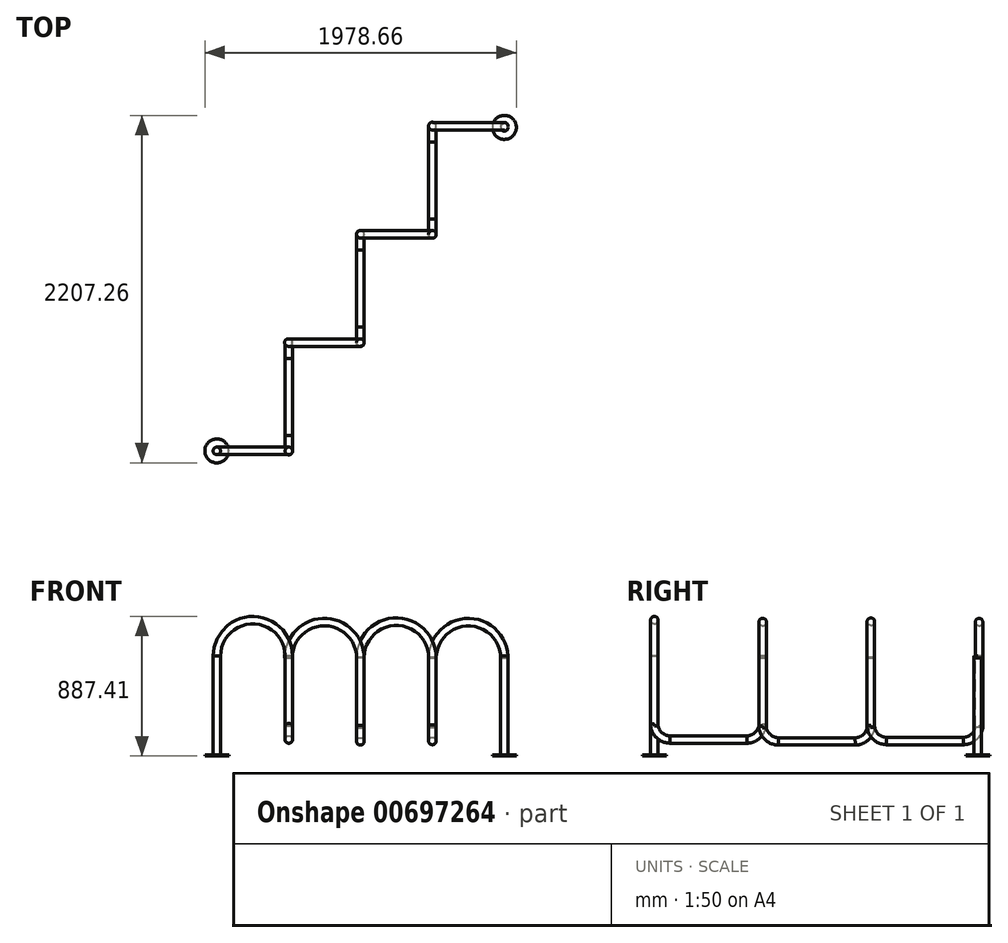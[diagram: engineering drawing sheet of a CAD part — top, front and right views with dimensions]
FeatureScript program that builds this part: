
annotation { "Feature Type Name" : "Feature", "Feature Type Description" : "" }
export const myFeature = defineFeature(function(context is Context, id is Id, definition is map)
    precondition{}
    {
        {
            var Q0;
            Q0=qCreatedBy(makeId("Top.planeOp"),FACE);
            var sketch = newSketch(context, id + "F0", { "sketchPlane" : qUnion([Q0])});
            skCircle(sketch, "E0", {"center": v(0, 0) * mm, "radius": 76.2 * mm});
            skCircle(sketch, "E1", {"center": v(0, 0) * mm, "radius": 23.81 * mm});
            skSolve(sketch);
        }
        {
            var Q0;
            Q0=makeQuery(id+"F0.imprint","IMPRINT",FACE,{"disambiguationData":[TD([[makeQuery(id+"F0.imprint","IMPRINT",EDGE,{"derivedFrom":sQuery(id+"F0.wireOp",EDGE,"E0")}),1.0]])]});
            extrude(context, id + "F1", {"entities" : qUnion([Q0]), "depth" : 6.35 * mm, "offsetDistance" : 25.4 * mm});
        }
        {
            var Q0;
            Q0=makeQuery(id+"F0.imprint","IMPRINT",FACE,{"disambiguationData":[TD([[makeQuery(id+"F0.imprint","IMPRINT",EDGE,{"derivedFrom":sQuery(id+"F0.wireOp",EDGE,"E1")}),1.0]])]});
            extrude(context, id + "F2", {"entities" : qUnion([Q0]), "operationType" : NewBodyOperationType.ADD, "depth" : 635 * mm, "offsetDistance" : 25.4 * mm});
        }
        {
            var Q0;
            Q0=qCreatedBy(makeId("Front.planeOp"),FACE);
            var sketch = newSketch(context, id + "F3", { "sketchPlane" : qUnion([Q0])});
            skArc(sketch, "E2", {"start": v(457.2, 635) * mm, "mid": v(228.6, 863.6) * mm, "end": v(0, 635) * mm});
            skLineSegment(sketch, "E3", {"start": v(0, 0) * mm, "end": v(0, 635) * mm});
            skLineSegment(sketch, "E4", {"start": v(457.2, 635) * mm, "end": v(457.2, 228.6) * mm});
            skLineSegment(sketch, "E5", {"start": v(228.6, 863.6) * mm, "end": v(228.6, 0) * mm, "construction": true});
            skLineSegment(sketch, "E6", {"start": v(228.6, 863.6) * mm, "end": v(951.54, 863.6) * mm, "construction": true});
            skSolve(sketch);
        }
        {
            var Q0;
            Q0=makeQuery(id+"F2.opExtrude","CAP_FACE",FACE,{"disambiguationData":[OSD([sQuery(id+"F0.wireOp",EDGE,"E1")])],"isStart":false});
            var Q1;
            Q1=sQuery(id+"F3.wireOp",EDGE,"E2");
            sweep(context, id + "F4", {"profiles" : qUnion([Q0]), "path" : qUnion([Q1])});
        }
        {
            var Q0;
            Q0=makeQuery(id+"F4.opSweep","CAP_FACE",FACE,{"disambiguationData":[OSD([sQuery(id+"F0.wireOp",EDGE,"E1"),sQuery(id+"F3.wireOp",VERTEX,"E2.start")])],"isStart":false});
            var sketch = newSketch(context, id + "F5", { "sketchPlane" : qUnion([Q0])});
            skCircle(sketch, "E7.0", {"center": v(457.2, 0) * mm, "radius": 23.81 * mm});
            skSolve(sketch);
        }
        {
            var Q0;
            Q0=qSketchRegion(id+"F5",true);
            extrude(context, id + "F6", {"entities" : qUnion([Q0]), "operationType" : NewBodyOperationType.ADD, "depth" : 444.5 * mm, "offsetDistance" : 25.4 * mm});
        }
        {
            var Q0;
            Q0=qCreatedBy(makeId("Right.planeOp"),FACE);
            cPlane(context, id + "F7", {"entities" : qUnion([Q0]), "cplaneType" : CPlaneType.OFFSET, "offset" : 457.2 * mm, "width" : 152.4 * mm, "height" : 152.4 * mm});
        }
        {
            var Q0;
            Q0=qCreatedBy(id+"F7.planeOp",FACE);
            var sketch = newSketch(context, id + "F8", { "sketchPlane" : qUnion([Q0])});
            skLineSegment(sketch, "E8", {"start": v(100.01, 106.8) * mm, "end": v(587.38, 106.8) * mm});
            skArc(sketch, "E9", {"start": v(0, 203.2) * mm, "mid": v(30.96, 135.23) * mm, "end": v(100.01, 106.8) * mm});
            skArc(sketch, "E10", {"start": v(587.38, 106.8) * mm, "mid": v(656.43, 135.23) * mm, "end": v(687.39, 203.2) * mm});
            skLineSegment(sketch, "E11", {"start": v(687.39, 635) * mm, "end": v(687.52, 203.2) * mm});
            skLineSegment(sketch, "E12.0", {"start": v(23.81, 635) * mm, "end": v(-23.81, 635) * mm});
            skLineSegment(sketch, "E13", {"start": v(0, 635) * mm, "end": v(687.39, 635) * mm, "construction": true});
            skLineSegment(sketch, "E14", {"start": v(711.2, 203.2) * mm, "end": v(663.58, 203.2) * mm, "construction": true});
            skLineSegment(sketch, "E15.0", {"start": v(23.81, 203.2) * mm, "end": v(-23.81, 203.2) * mm});
            skSolve(sketch);
        }
        {
            var Q0;
            Q0=makeQuery(id+"F6.opExtrude","CAP_FACE",FACE,{"disambiguationData":[OSD([sQuery(id+"F5.wireOp",EDGE,"E7.0")])],"isStart":false});
            var Q1;
            Q1=sQuery(id+"F8.wireOp",EDGE,"E10");
            var Q2;
            Q2=sQuery(id+"F8.wireOp",EDGE,"E8");
            var Q3;
            Q3=sQuery(id+"F8.wireOp",EDGE,"E9");
            sweep(context, id + "F9", {"operationType" : NewBodyOperationType.ADD, "profiles" : qUnion([Q0]), "path" : qUnion([Q1, Q2, Q3])});
        }
        {
            var Q0;
            Q0=qCreatedBy(makeId("Top.planeOp"),FACE);
            var Q1;
            Q1=sQuery(id+"F8.wireOp",VERTEX,"E11.start");
            cPlane(context, id + "F10", {"entities" : qUnion([Q0, Q1]), "cplaneType" : CPlaneType.PLANE_POINT, "offset" : 25.4 * mm, "width" : 152.4 * mm, "height" : 152.4 * mm});
        }
        {
            var Q0;
            Q0=qCreatedBy(id+"F10.planeOp",FACE);
            var sketch = newSketch(context, id + "F11", { "sketchPlane" : qUnion([Q0])});
            skCircle(sketch, "E16", {"center": v(457.2, 687.39) * mm, "radius": 23.81 * mm});
            skSolve(sketch);
        }
        {
            var Q0;
            Q0=makeQuery(id+"F11.imprint","IMPRINT",FACE,{"disambiguationData":[TD([[makeQuery(id+"F11.imprint","IMPRINT",EDGE,{"derivedFrom":sQuery(id+"F11.wireOp",EDGE,"E16")}),1.0]])]});
            extrude(context, id + "F12", {"entities" : qUnion([Q0]), "operationType" : NewBodyOperationType.ADD, "oppositeDirection" : true, "depth" : 444.5 * mm, "offsetDistance" : 25.4 * mm});
        }
        {
            var Q0;
            Q0=makeQuery(id+"F4.opSweep","SWEPT_BODY",BODY,{"disambiguationData":[OSD([sQuery(id+"F0.wireOp",EDGE,"E1"),sQuery(id+"F3.wireOp",EDGE,"E2")])]});
            transform(context, id + "F13", {"entities" : qUnion([Q0]), "transformType" : TransformType.TRANSLATION_3D, "dx" : 454.4 * mm, "dy" : 688.34 * mm, "dz" : -11.94 * mm, "makeCopy" : true});
        }
        {
            var Q0;
            Q0=makeQuery(id+"F13.opPattern","COPY",BODY,{"derivedFrom":makeQuery(id+"F4.opSweep","SWEPT_BODY",BODY,{"disambiguationData":[OSD([sQuery(id+"F0.wireOp",EDGE,"E1"),sQuery(id+"F3.wireOp",EDGE,"E2")])]}),"instanceName":"1"});
            transform(context, id + "F14", {"entities" : qUnion([Q0]), "transformType" : TransformType.TRANSLATION_3D, "dx" : 457.2 * mm, "dy" : 687.4 * mm, "dz" : 2.54 * mm, "makeCopy" : true});
        }
        {
            var Q0;
            Q0=qCreatedBy(makeId("Front.planeOp"),FACE);
            cPlane(context, id + "F15", {"entities" : qUnion([Q0]), "cplaneType" : CPlaneType.OFFSET, "offset" : 685.8 * mm, "width" : 152.4 * mm, "height" : 152.4 * mm});
        }
        {
            var Q0;
            Q0=qCreatedBy(id+"F15.planeOp",FACE);
            var sketch = newSketch(context, id + "F16", { "sketchPlane" : qUnion([Q0])});
            skArc(sketch, "E17.0", {"start": v(457.2, 635) * mm, "mid": v(228.6, 863.6) * mm, "end": v(0, 635) * mm});
            skLineSegment(sketch, "E18.0", {"start": v(-23.81, 635) * mm, "end": v(23.81, 635) * mm});
            skSolve(sketch);
        }
        {
            var Q0;
            Q0=qCreatedBy(makeId("Top.planeOp"),FACE);
            cPlane(context, id + "F17", {"entities" : qUnion([Q0]), "cplaneType" : CPlaneType.OFFSET, "offset" : 635 * mm, "width" : 152.4 * mm, "height" : 152.4 * mm});
        }
        {
            var Q0;
            Q0=qCreatedBy(id+"F17.planeOp",FACE);
            var sketch = newSketch(context, id + "F18", { "sketchPlane" : qUnion([Q0])});
            skLineSegment(sketch, "E19.0", {"start": v(-23.81, -685.8) * mm, "end": v(23.81, -685.8) * mm});
            skCircle(sketch, "E20", {"center": v(0, -685.8) * mm, "radius": 23.81 * mm});
            skSolve(sketch);
        }
        {
            var Q0;
            {var subQ0=sQuery(id+"F18.wireOp",EDGE,"E19.0");Q0=makeQuery(id+"F18.imprint","IMPRINT",FACE,{"disambiguationData":[TD([[makeQuery(id+"F18.imprint","IMPRINT",EDGE,{"derivedFrom":subQ0}),-1.0]])]});}
            var Q1;
            {var subQ0=sQuery(id+"F18.wireOp",EDGE,"E19.0");Q1=makeQuery(id+"F18.imprint","IMPRINT",FACE,{"disambiguationData":[TD([[makeQuery(id+"F18.imprint","IMPRINT",EDGE,{"derivedFrom":subQ0}),1.0]])]});}
            var Q2;
            Q2=sQuery(id+"F16.wireOp",EDGE,"E17.0");
            sweep(context, id + "F19", {"profiles" : qUnion([Q0, Q1]), "path" : qUnion([Q2])});
        }
        {
            var Q0;
            Q0=makeQuery(id+"F19.opSweep","SWEPT_BODY",BODY,{"disambiguationData":[OSD([sQuery(id+"F16.wireOp",EDGE,"E17.0"),sQuery(id+"F18.wireOp",EDGE,"E20")])]});
            transform(context, id + "F20", {"entities" : qUnion([Q0]), "transformType" : TransformType.TRANSLATION_3D, "dx" : 1369.06 * mm, "dy" : 2748.28 * mm, "dz" : -12.7 * mm, "makeCopy" : false});
        }
        {
            var Q0;
            Q0=makeQuery(id+"F1.opExtrude","SWEPT_BODY",BODY,{"disambiguationData":[OSD([sQuery(id+"F0.wireOp",EDGE,"E0"),sQuery(id+"F0.wireOp",EDGE,"E1")])]});
            transform(context, id + "F21", {"entities" : qUnion([Q0]), "transformType" : TransformType.TRANSLATION_3D, "dx" : 1826.26 * mm, "dy" : 2054.86 * mm, "dz" : 0 * mm, "makeCopy" : true});
        }
    });
